# Revit family: Bath-Alcove-Whirlpool-KOHLER-Windward-K-1112_1
name_source: partatom
category: Plumbing Fixtures
units: mm (PartAtom-declared; Revit-internal decimal feet)

## family parameters
Cut with Voids When Loaded = No
Host = Face
OmniClass Number = 23.31.15.00
OmniClass Title = Bathtubs
Part Type = Normal
Room Calculation Point = No
Round Connector Dimension = Use Diameter
Shared = No

## types (2) — shared parameters
ADA Compliant = No
Amplifer Electrical Connector = Amplifer Electrical Connector
Apparent Load = 1800 VA
Assembly Code = D2010500
Blower Electrical Connector = Blower Electrical Connector
CW Connection = No
Cold Water Inlet = Cold Water Inlet
Date Modified = 08/18/2022
Default Elevation = 0"
Drain Included = No
Electrical Connector = Yes
Electrical Note = One dedicated circuit required, protected with Class A GroundFault Circuit-Interrupter (GFCI)
Finish = KOHLER-Acrylic-0-White
HW Connection = No
Heater Electrical Connector = Heater Electrical Connector
Height = 22 1/4"
Hot Water Inlet = Hot Water Inlet
Length = 60"
Manufacturer = Kohler Co.
Master Format 2014 = 22 41 19
Master Format 2014 Name = Residential Bathtubs
Material = Acrylic
Product Documentation Link = https://www.us.kohler.com
Product Name = Windward
Product Page URL = https://www.us.kohler.com
Pump Electrical Connector = Pump Electrical Connector
URL = https://www.us.kohler.com
Vent Connection = No
Voltage = 120 V
Waste Connection = Yes
Waste Water Outlet = Waste Water Outlet
WaterSense Certified = No
Width = 42"

## per-type parameters (varying)
| type | Connector Distance | Description | Electrical Connector Distance | Left Hand Drain | Model | Right Hand Drain | Type |
| Left Drain, 0-White | 38 3/8" | 60 Inch x 42 Inch alcove whirlpool with integral apron and left-hand drain | 40 13/16" | Yes | K-1112-LA-0 | No | 1 |
| Right Drain, 0-White | 0" | 60 Inch x 42 Inch alcove whirlpool with integral apron and right-hand drain | 0" | No | K-1112-RA-0 | Yes | 2 |

## geometry (parser evidence)
native form markers: Sweep x5
no freeform markers — native parametric forms only
